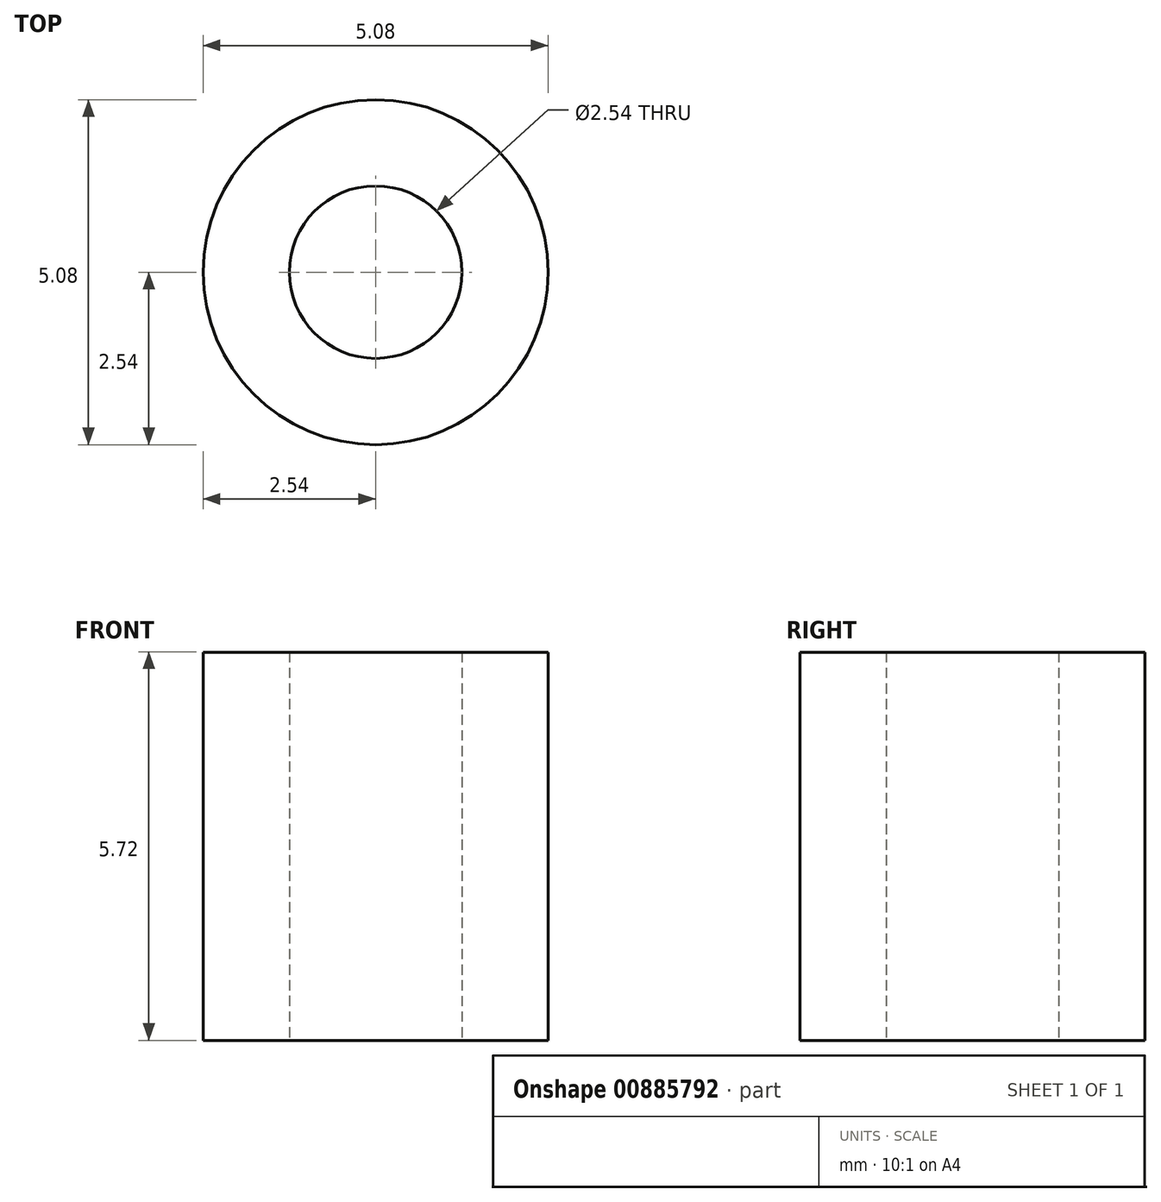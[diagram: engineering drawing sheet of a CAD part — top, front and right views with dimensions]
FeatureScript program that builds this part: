
annotation { "Feature Type Name" : "Feature", "Feature Type Description" : "" }
export const myFeature = defineFeature(function(context is Context, id is Id, definition is map)
    precondition{}
    {
        {
            var Q0;
            Q0=qCreatedBy(makeId("Top.planeOp"),FACE);
            var sketch = newSketch(context, id + "F0", { "sketchPlane" : qUnion([Q0])});
            skCircle(sketch, "E0", {"center": v(0, 0) * mm, "radius": 2.54 * mm});
            skCircle(sketch, "E1", {"center": v(0, 0) * mm, "radius": 1.27 * mm});
            skSolve(sketch);
        }
        {
            var Q0;
            Q0=makeQuery(id+"F0.imprint","IMPRINT",FACE,{"disambiguationData":[TD([[makeQuery(id+"F0.imprint","IMPRINT",EDGE,{"derivedFrom":sQuery(id+"F0.wireOp",EDGE,"E0")}),1.0]])]});
            extrude(context, id + "F1", {"entities" : qUnion([Q0]), "depth" : 5.7 * mm, "offsetDistance" : 25.4 * mm});
        }
    });
